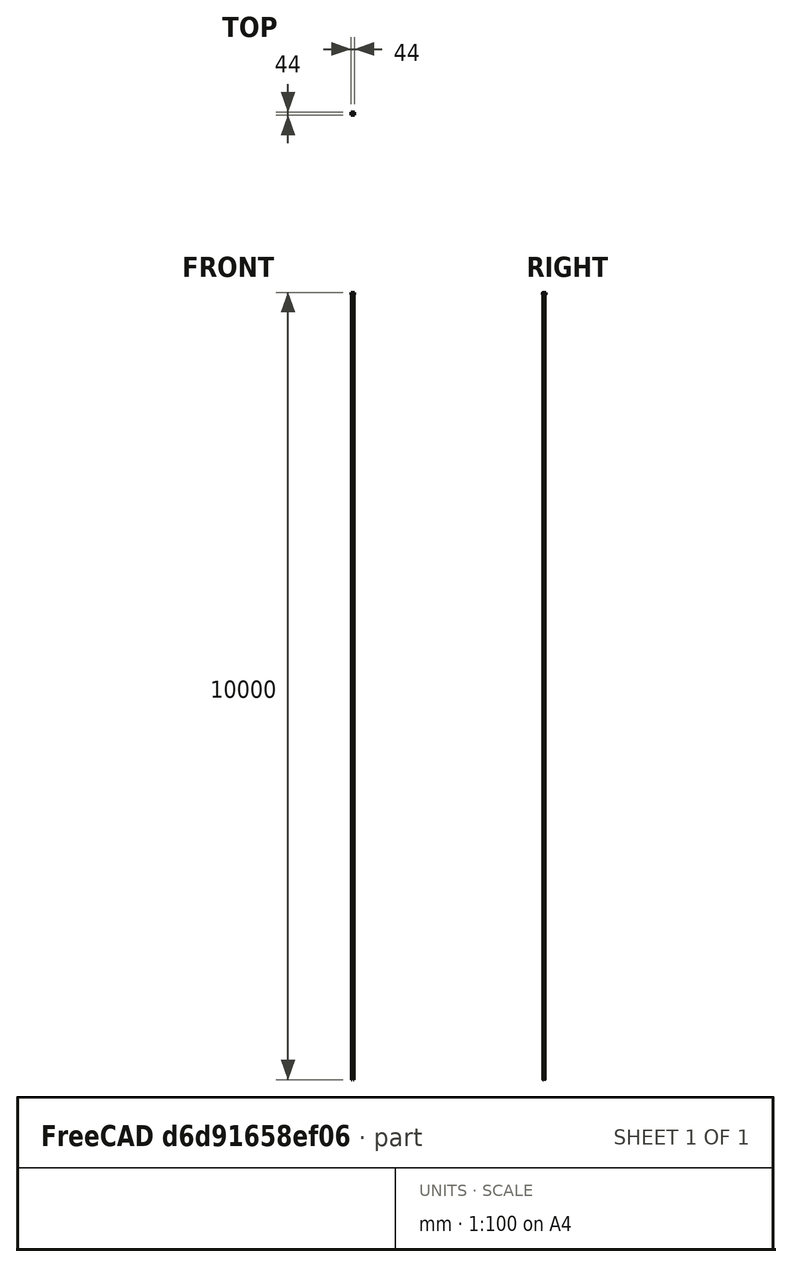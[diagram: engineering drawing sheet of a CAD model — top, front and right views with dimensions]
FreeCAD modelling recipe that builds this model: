
FCSTD DOCUMENT  (FreeCAD 0.16R)
Label: SquashBallFoot_2020_90
License: All rights reserved
LicenseURL: http://en.wikipedia.org/wiki/All_rights_reserved
objects: Sketcher::SketchObject×5, Part::Sphere×2, Part::Cut×2, Part::Box×1, Part::Loft×1, Part::MultiFuse×1, PartDesign::Pad×1, PartDesign::Chamfer×1, PartDesign::Pocket×1
note: 17 computed .brp shape members not serialized (recipe doc carries the construction recipe); baked Part::Feature solids carry a one-line shape summary decoded from their .brp

FEATURE [Part::Sphere] Sphere
  Angle1 = -90
  Angle2 = 90
  Angle3 = 360
  Radius = 22
FEATURE [Part::Box] Box  label="Cube"
  Height = 44
  Length = 44
  Placement = pos=(-22,-22,-46) rot=(0,0,1;0rad)
  Width = 44
FEATURE [Part::Cut] Cut
  Base = -> Sphere
  Tool = -> Box
FEATURE [Part::Sphere] Sphere001
  Angle1 = -90
  Angle2 = 90
  Angle3 = 360
  Radius = 20
FEATURE [Sketcher::SketchObject] Sketch
  sketch-geometry (1):
    g0: Circle CenterX=0 CenterY=0 CenterZ=0 NormalX=0 NormalY=0 NormalZ=1 Radius=22
  constraints (2):
    c: Coincident(g0,g-1)
    c: Radius(g0) = 22
FEATURE [Sketcher::SketchObject] Sketch001
  Placement = pos=(0,0,25) rot=(0,0,1;0rad)
  sketch-geometry (4):
    g0: LineSegment StartX=-22 StartY=22 StartZ=0 EndX=22 EndY=22 EndZ=0
    g1: LineSegment StartX=22 StartY=22 StartZ=0 EndX=22 EndY=-22 EndZ=0
    g2: LineSegment StartX=22 StartY=-22 StartZ=0 EndX=-22 EndY=-22 EndZ=0
    g3: LineSegment StartX=-22 StartY=-22 StartZ=0 EndX=-22 EndY=22 EndZ=0
  constraints (11):
    c: Coincident(g0,g1)
    c: Coincident(g1,g2)
    c: Coincident(g2,g3)
    c: Coincident(g3,g0)
    c: Horizontal(g0)
    c: Horizontal(g2)
    c: Vertical(g1)
    c: Vertical(g3)
    c: Symmetric(g0,g1,g-1)
    c: Equal(g0,g1)
    c: DistanceX(g0,g0) = 44
FEATURE [Part::Loft] Loft
  Closed = false
  Ruled = false
  Sections = -> [Sketch,Sketch001]
  Solid = true
FEATURE [Part::MultiFuse] Fusion
  Shapes = -> [Loft,Cut]
FEATURE [Part::Cut] Cut001
  Base = -> Fusion
  Tool = -> Sphere001
FEATURE [Sketcher::SketchObject] Sketch003  label="HeadHoles"
  Placement = pos=(0,0,-2) rot=(1,0,0;3.14159rad)
  sketch-geometry (2):
    g0: Circle CenterX=-11 CenterY=11 CenterZ=0 NormalX=0 NormalY=0 NormalZ=1 Radius=4
    g1: Circle CenterX=11 CenterY=-11 CenterZ=0 NormalX=0 NormalY=0 NormalZ=1 Radius=4
  constraints (5):
    c: Equal(g0,g1)
    c: Radius(g0) = 4
    c: Symmetric(g1,g0,g-1)
    c: DistanceX(g0,g-1) = 11
    c: DistanceY(g-1,g0) = 11
FEATURE [Sketcher::SketchObject] Sketch004
  Placement = pos=(0,0,25) rot=(0,0,1;0rad)
  Support = -> Cut001 [Face1]
  sketch-geometry (10):
    g0: LineSegment [constr] StartX=-12 StartY=22 StartZ=0 EndX=-12 EndY=-22 EndZ=0
    g1: LineSegment [constr] StartX=-22 StartY=12 StartZ=0 EndX=22 EndY=12 EndZ=0
    g2: LineSegment StartX=-14 StartY=-1 StartZ=0 EndX=-10 EndY=-1 EndZ=0
    g3: LineSegment StartX=-10 StartY=-1 StartZ=0 EndX=-10 EndY=-22 EndZ=0
    g4: LineSegment StartX=-10 StartY=-22 StartZ=0 EndX=-14 EndY=-22 EndZ=0
    g5: LineSegment StartX=-14 StartY=-22 StartZ=0 EndX=-14 EndY=-1 EndZ=0
    g6: LineSegment StartX=0 StartY=14 StartZ=0 EndX=22 EndY=14 EndZ=0
    g7: LineSegment StartX=22 StartY=14 StartZ=0 EndX=22 EndY=10 EndZ=0
    g8: LineSegment StartX=22 StartY=10 StartZ=0 EndX=0 EndY=10 EndZ=0
    g9: LineSegment StartX=0 StartY=10 StartZ=0 EndX=0 EndY=14 EndZ=0
  constraints (29):
    c: Symmetric(g0,g0,g-1)
    c: DistanceX(g0,g-1) = 12
    c: Symmetric(g1,g1,g-2)
    c: Equal(g0,g1)
    c: DistanceX(g1,g1) = 44
    c: DistanceY(g-1,g1) = 12
    c: Coincident(g2,g3)
    c: Coincident(g3,g4)
    c: Coincident(g4,g5)
    c: Coincident(g5,g2)
    c: Horizontal(g2)
    c: Horizontal(g4)
    c: Vertical(g3)
    c: Vertical(g5)
    c: Symmetric(g2,g2,g0)
    c: DistanceX(g4,g4) = 4
    c: Coincident(g6,g7)
    c: Coincident(g7,g8)
    c: Coincident(g8,g9)
    c: Coincident(g9,g6)
    c: Horizontal(g6)
    c: Horizontal(g8)
    c: Vertical(g7)
    c: Vertical(g9)
    c: Symmetric(g8,g6,g1)
    c: DistanceX(g6,g6) = 22
    c: DistanceY(g7,g7) = 4
    c: DistanceY(g4,g-1) = 22
    c: DistanceY(g5,g5) = 21
FEATURE [PartDesign::Pad] Pad
  Length = 1.001
  Length2 = 100
  Sketch = -> Sketch004
  Type = 0
FEATURE [PartDesign::Chamfer] Chamfer
  Base = -> Pad [Edge19,Edge18,Edge24,Edge25,Edge20,Edge23]
  Size = 1
FEATURE [Sketcher::SketchObject] Sketch002  label="ScrewHoles"
  Placement = pos=(0,0,26.001) rot=(0,0,1;0rad)
  Support = -> Chamfer [Face25]
  sketch-geometry (6):
    g0: LineSegment [constr] StartX=-22 StartY=22 StartZ=0 EndX=22 EndY=22 EndZ=0
    g1: LineSegment [constr] StartX=22 StartY=22 StartZ=0 EndX=22 EndY=-22 EndZ=0
    g2: LineSegment [constr] StartX=22 StartY=-22 StartZ=0 EndX=-22 EndY=-22 EndZ=0
    g3: LineSegment [constr] StartX=-22 StartY=-22 StartZ=0 EndX=-22 EndY=22 EndZ=0
    g4: Circle CenterX=-12 CenterY=-12 CenterZ=0 NormalX=0 NormalY=0 NormalZ=1 Radius=2.2
    g5: Circle CenterX=12 CenterY=12 CenterZ=0 NormalX=0 NormalY=0 NormalZ=1 Radius=2.2
  constraints (16):
    c: Coincident(g0,g1)
    c: Coincident(g1,g2)
    c: Coincident(g2,g3)
    c: Coincident(g3,g0)
    c: Horizontal(g0)
    c: Horizontal(g2)
    c: Vertical(g1)
    c: Vertical(g3)
    c: Symmetric(g0,g1,g-1)
    c: Equal(g0,g1)
    c: DistanceX(g0,g0) = 44
    c: Equal(g4,g5)
    c: Radius(g4) = 2.2
    c: Symmetric(g5,g4,g-1)
    c: DistanceY(g4,g-1) = 12
    c: DistanceX(g4,g-1) = 12
FEATURE [PartDesign::Pocket] Pocket
  Length = 5
  Sketch = -> Sketch002
  Type = 1
